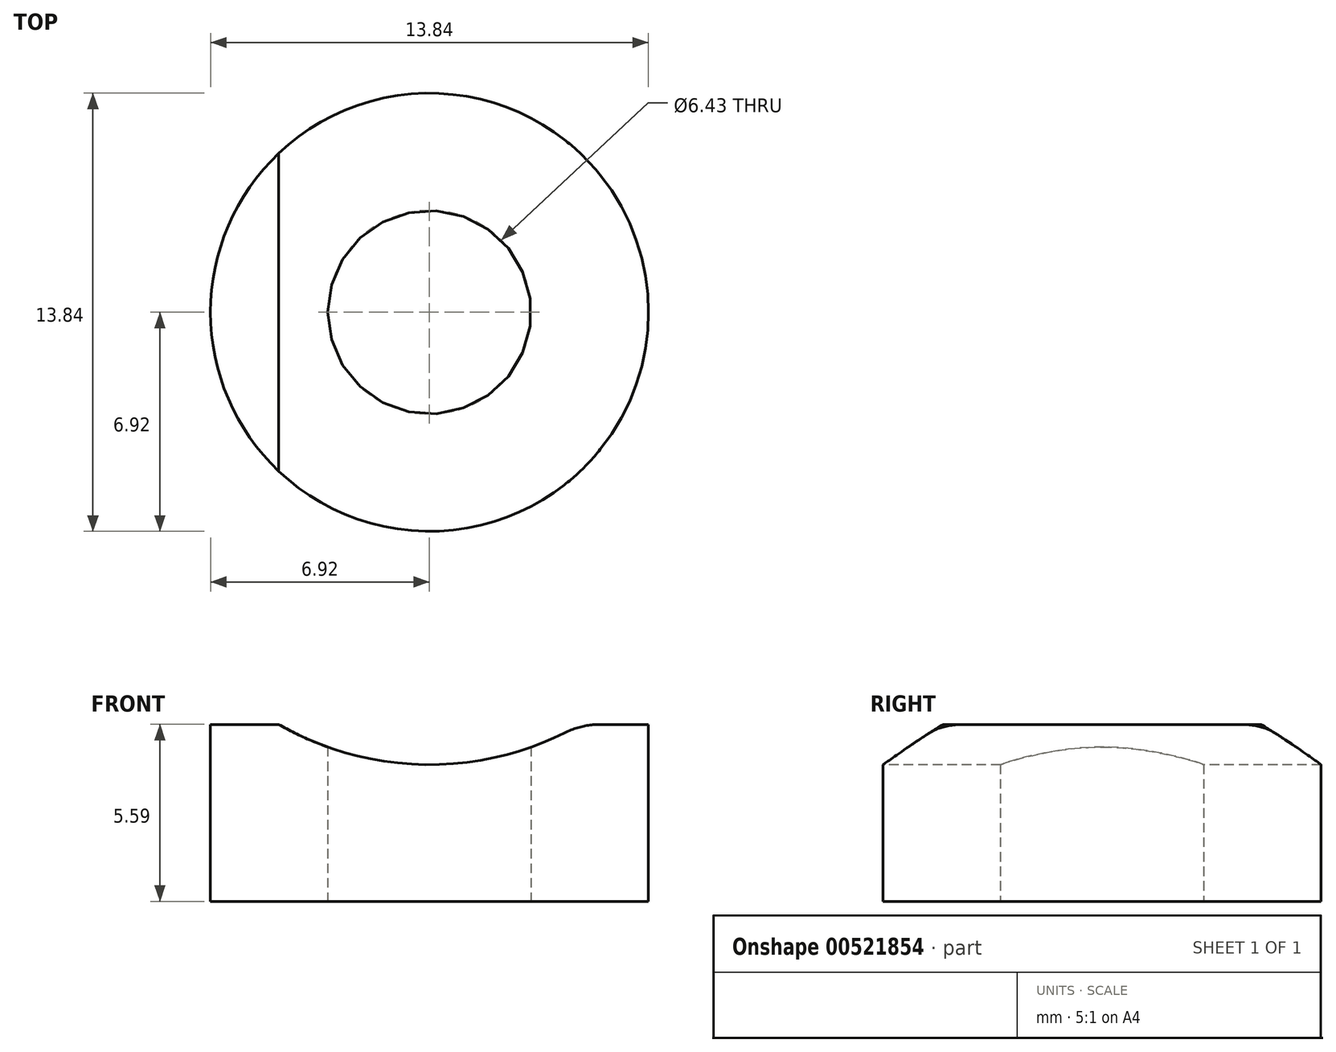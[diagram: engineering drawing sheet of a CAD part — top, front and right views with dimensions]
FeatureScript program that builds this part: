
annotation { "Feature Type Name" : "Feature", "Feature Type Description" : "" }
export const myFeature = defineFeature(function(context is Context, id is Id, definition is map)
    precondition{}
    {
        {
            var Q0;
            Q0=qCreatedBy(makeId("Top.planeOp"),FACE);
            var sketch = newSketch(context, id + "F0", { "sketchPlane" : qUnion([Q0])});
            skCircle(sketch, "E0", {"center": v(0, 0) * mm, "radius": 6.92 * mm});
            skCircle(sketch, "E1", {"center": v(0, 0) * mm, "radius": 3.21 * mm});
            skSolve(sketch);
        }
        {
            var Q0;
            Q0 = qSketchRegion(id + "F0", true);
            extrude(context, id + "F1", {"entities" : qUnion([Q0]), "depth" : 5.6 * mm, "offsetDistance" : 25.4 * mm});
        }
        {
            var Q0;
            Q0=qCreatedBy(makeId("Front.planeOp"),FACE);
            var sketch = newSketch(context, id + "F2", { "sketchPlane" : qUnion([Q0])});
            skArc(sketch, "E2", {"start": v(-4.76, 5.59) * mm, "mid": v(0, 4.32) * mm, "end": v(4.76, 5.59) * mm});
            skLineSegment(sketch, "E3", {"start": v(-4.76, 5.59) * mm, "end": v(4.76, 5.59) * mm});
            skSolve(sketch);
        }
        {
            var Q0;
            Q0 = qSketchRegion(id + "F2", true);
            extrude(context, id + "F3", {"entities" : qUnion([Q0]), "operationType" : NewBodyOperationType.REMOVE, "endBound" : BoundingType.THROUGH_ALL, "oppositeDirection" : true, "depth" : 25.4 * mm, "offsetDistance" : 25.4 * mm, "hasSecondDirection" : true, "secondDirectionBound" : SecondDirectionBoundingType.THROUGH_ALL, "secondDirectionOppositeDirection" : false, "secondDirectionDepth" : 25.4 * mm});
        }
        {
            var Q0;
            {var subQ0=sQuery(id+"F2.wireOp",EDGE,"E3");var subQ1=sQuery(id+"F2.wireOp",EDGE,"E2");Q0=makeQuery(id+"F3.boolean.opBoolean","COPY",EDGE,{"derivedFrom":makeQuery(id+"F3.opExtrude","SWEPT_EDGE",EDGE,{"disambiguationData":[OSD([subQ1,subQ0]),TDD([makeQuery(id+"F2.imprint","INTERSECT",VERTEX,{"disambiguationData":[OD(0.0)],"derivedFrom":[subQ1,subQ0]})])]})});}
            var Q1;
            {var subQ0=sQuery(id+"F2.wireOp",EDGE,"E3");var subQ1=sQuery(id+"F2.wireOp",EDGE,"E2");Q1=makeQuery(id+"F3.boolean.opBoolean","COPY",EDGE,{"derivedFrom":makeQuery(id+"F3.opExtrude","SWEPT_EDGE",EDGE,{"disambiguationData":[OSD([subQ1,subQ0]),TDD([makeQuery(id+"F2.imprint","INTERSECT",VERTEX,{"disambiguationData":[OD(1.0)],"derivedFrom":[subQ1,subQ0]})])]})});}
            fillet(context, id + "F4", {"entities" : qUnion([Q0, Q1]), "radius" : 2.54 * mm, "tangentPropagation" : true, "allowEdgeOverflow" : false});
        }
    });
